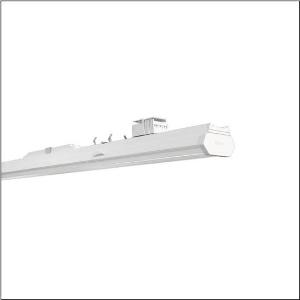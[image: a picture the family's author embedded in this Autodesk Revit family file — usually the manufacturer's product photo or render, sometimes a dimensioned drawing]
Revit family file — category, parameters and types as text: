
# Revit family: licross_r__21_protected_mo_52td12dn4a5g_44fa
name_source: partatom
category: Lighting Fixtures
units: mm (PartAtom-declared; Revit-internal decimal feet)

## family parameters
Cut with Voids When Loaded = No
Host = Face
Light Source = No
Part Type = Normal
Room Calculation Point = No
Round Connector Dimension = Use Diameter
Shared = No

## types (1)
- --- (1 x LED, 10700 lm, 62 W, 4000K)
    Apparent Load = 62 VA
    CIE Flux Codes = 73 92 98 99 100
    Color Rendering = 80
    Color Temperature = 4000K
    Default Elevation = 1800 mm
    Description = Licross® 21 Protected MO, luminaire insert, of sheet steel, galvanised, coil coated, white, length: 1.500mm, width: 90mm, height: 103mm, LED rated luminous flux: 10.700lm, light colour: 840, control gear: DALI 2, with plug, 5-pole, with phase selection, mains connection: 220..240V, AC, 50/60Hz, rated input power: 62W, halogen-free wiring, primary light control with lens, of plastic, primary optical cover: cover, of PMMA, light emission: direct distribution, primary light characteristic: symmetric, protection rating (complete): IP54, insulation class (complete): insulation class I (protective earthing), certification: CE, ENEC, VDE, UKCA, protection symbol: D if used in an environment with non-conductive dust loads with corresponding accessories, impact resistance: IK06, permissible ambient temperature for indoor applications: -25..+35°C, corresponds to IFS (International Featured Standards) requirements for safety and quality in the food industry, reducing of maximum allowable ambient temperature of 5°C with ceiling mounting, LABS conformity tested according to VDMA 24364:2018-05, packaging unit: 1 piece
    Height = 92 mm
    Lamp = 1 x LED
    Lamp Light Flux = 10700 lm
    Lamp Power = 62 W
    Lamp count = 1
    Length = 1500 mm
    Luminous efficacy = 173 lm/W
    Manufacturer = Siteco
    ModVariant = No
    Model = 52TD12DN4A5G
    Mounting Place = Ceiling
    Mounting Type = Pendant
    Number of Poles = 1
    OnlyDefault = Yes
    Power Factor = 1
    Product Name = Licross® 21 Protected MO
    Product group = luminaire insert
    ProductGroupID = 901
    Protection Class = Protection class I
    Protection Degree = IP 54
    RLX_Detail_Level = 1
    RLX_Emergency_Light_Flux = 0 lm
    RLX_Emergency_Type = 0
    RLX_Emergency_Type_DB = No
    RlxData = <blob elided: 24393 chars, md5=b35179d4>
    Socket = socket
    Standby Power = 0 W
    System Light Flux = 10700 lm
    System Power = 62 W
    Type Comments = factory setting: luminous flux: 100 % | dim-lin: 254 | 418 mA
    Type Image = l_1256148.jpg
    URL = http://relux.com
    VarID = @adj_078455
    Voltage = 0 V
    Weight = 0.00 kg
    Width = 88 mm

## geometry (parser evidence)
native form markers: Blend x4, Sweep x12
no freeform markers — native parametric forms only
